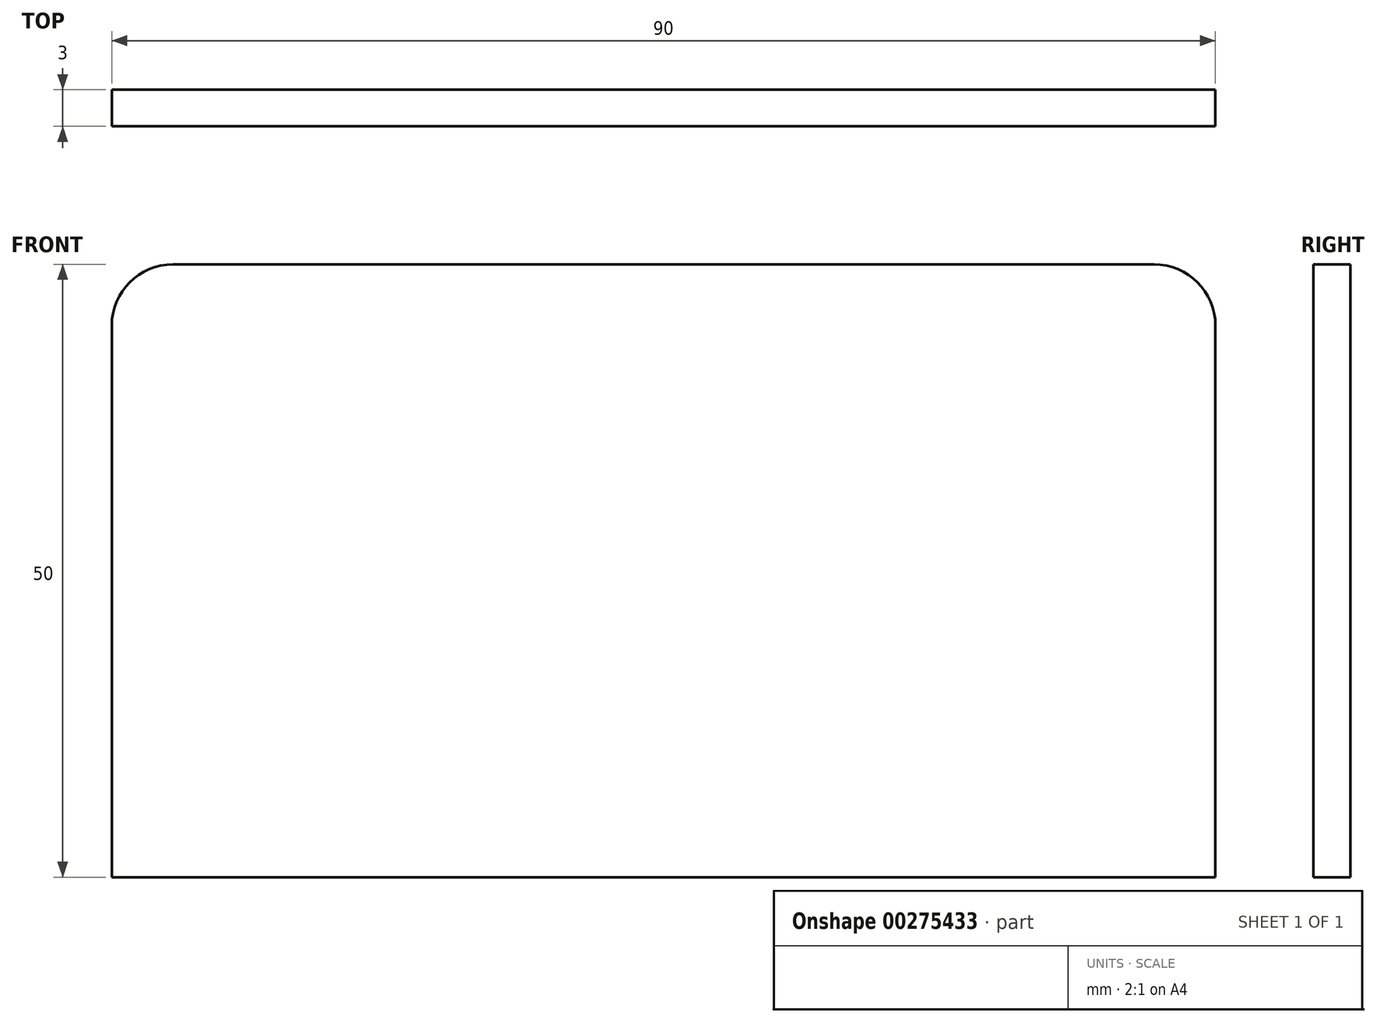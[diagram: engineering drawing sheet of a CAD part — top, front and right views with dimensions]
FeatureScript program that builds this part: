
annotation { "Feature Type Name" : "Feature", "Feature Type Description" : "" }
export const myFeature = defineFeature(function(context is Context, id is Id, definition is map)
    precondition{}
    {
        {
            var Q0;
            Q0=qCreatedBy(makeId("Front.planeOp"),FACE);
            var sketch = newSketch(context, id + "F0", { "sketchPlane" : qUnion([Q0])});
            skLineSegment(sketch, "E0.bottom", {"start": v(-24.1, -4.97) * mm, "end": v(55.9, -4.97) * mm});
            skLineSegment(sketch, "E0.top", {"start": v(-29.1, -54.97) * mm, "end": v(60.9, -54.97) * mm});
            skLineSegment(sketch, "E0.left", {"start": v(-29.1, -9.97) * mm, "end": v(-29.1, -54.97) * mm});
            skLineSegment(sketch, "E0.right", {"start": v(60.9, -9.97) * mm, "end": v(60.9, -54.97) * mm});
            skPoint(sketch, "E1.visualSharp", {"position": v(-29.1, -4.97) * mm});
            skArc(sketch, "E1.filletArc", {"start": v(-24.1, -4.97) * mm, "mid": v(-27.64, -6.44) * mm, "end": v(-29.1, -9.97) * mm});
            skPoint(sketch, "E2.visualSharp", {"position": v(60.9, -4.97) * mm});
            skArc(sketch, "E2.filletArc", {"start": v(60.9, -9.97) * mm, "mid": v(59.43, -6.44) * mm, "end": v(55.9, -4.97) * mm});
            skSolve(sketch);
        }
        {
            var Q0;
            Q0=makeQuery(id+"F0.imprint","IMPRINT",FACE,{"disambiguationData":[TD([[makeQuery(id+"F0.imprint","IMPRINT",EDGE,{"derivedFrom":sQuery(id+"F0.wireOp",EDGE,"E0.bottom")}),-1.0]])]});
            extrude(context, id + "F1", {"entities" : qUnion([Q0]), "depth" : 3 * mm, "offsetDistance" : 25 * mm});
        }
    });
